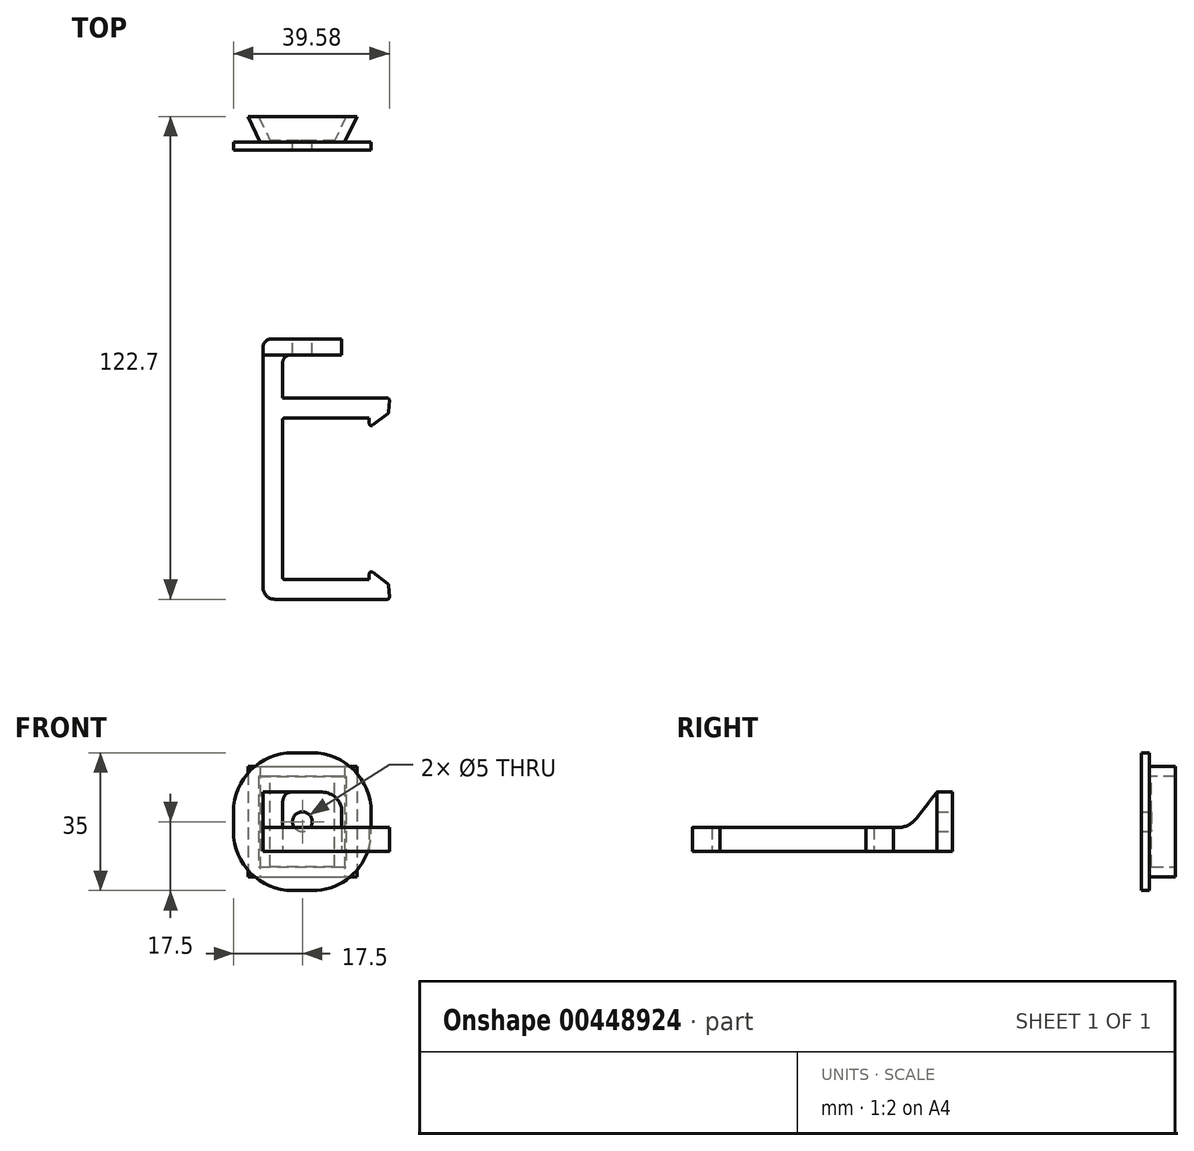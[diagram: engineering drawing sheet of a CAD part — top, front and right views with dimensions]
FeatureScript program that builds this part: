
annotation { "Feature Type Name" : "Feature", "Feature Type Description" : "" }
export const myFeature = defineFeature(function(context is Context, id is Id, definition is map)
    precondition{}
    {
        {
            var Q0;
            Q0=qCreatedBy(makeId("Top.planeOp"),FACE);
            var sketch = newSketch(context, id + "F0", { "sketchPlane" : qUnion([Q0])});
            skLineSegment(sketch, "E0.bottom", {"start": v(11, -20.55) * mm, "end": v(-11, -20.55) * mm});
            skLineSegment(sketch, "E0.top", {"start": v(11, 20.55) * mm, "end": v(-11, 20.55) * mm});
            skLineSegment(sketch, "E0.right", {"start": v(-11, -20.55) * mm, "end": v(-11, 20.55) * mm});
            skPoint(sketch, "E0.middle", {"position": v(0, 0) * mm});
            skLineSegment(sketch, "E1.0", {"start": v(11.44, -25.55) * mm, "end": v(-16, -25.55) * mm});
            skLineSegment(sketch, "E1.1", {"start": v(-16, -25.55) * mm, "end": v(-16, 25.55) * mm});
            skLineSegment(sketch, "E1.2", {"start": v(11.44, 25.55) * mm, "end": v(-16, 25.55) * mm});
            skLineSegment(sketch, "E2", {"start": v(11, 20.55) * mm, "end": v(11, 18.05) * mm});
            skLineSegment(sketch, "E3", {"start": v(11, 18.05) * mm, "end": v(20.79, 25.55) * mm});
            skLineSegment(sketch, "E4", {"start": v(20.79, 25.55) * mm, "end": v(11.44, 25.55) * mm});
            skLineSegment(sketch, "E5", {"start": v(-46.78, 0) * mm, "end": v(45.2, 0) * mm, "construction": true});
            skLineSegment(sketch, "E6.MirrorCS", {"start": v(11, -18.05) * mm, "end": v(20.79, -25.55) * mm});
            skLineSegment(sketch, "E7.MirrorCS", {"start": v(20.79, -25.55) * mm, "end": v(11.44, -25.55) * mm});
            skLineSegment(sketch, "E8.MirrorCS", {"start": v(11, -20.55) * mm, "end": v(11, -18.05) * mm});
            skLineSegment(sketch, "E9", {"start": v(16.11, 25.55) * mm, "end": v(15.9, 21.8) * mm});
            skLineSegment(sketch, "E10.MirrorCS", {"start": v(16.11, -25.55) * mm, "end": v(15.9, -21.8) * mm});
            skSolve(sketch);
        }
        {
            var Q0;
            Q0=makeQuery(id+"F0.imprint","IMPRINT",FACE,{"disambiguationData":[TD([[makeQuery(id+"F0.imprint","IMPRINT",EDGE,{"derivedFrom":sQuery(id+"F0.wireOp",EDGE,"E0.bottom")}),1.0]])]});
            extrude(context, id + "F1", {"entities" : qUnion([Q0]), "depth" : 6 * mm});
        }
        {
            var Q0;
            Q0=makeQuery(id+"F1.opExtrude","CAP_FACE",FACE,{"disambiguationData":[OSD([sQuery(id+"F0.wireOp",EDGE,"E0.bottom"),sQuery(id+"F0.wireOp",EDGE,"E0.top"),sQuery(id+"F0.wireOp",EDGE,"E0.right"),sQuery(id+"F0.wireOp",EDGE,"E1.0"),sQuery(id+"F0.wireOp",EDGE,"E1.1"),sQuery(id+"F0.wireOp",EDGE,"E1.2"),sQuery(id+"F0.wireOp",EDGE,"E2"),sQuery(id+"F0.wireOp",EDGE,"E3"),sQuery(id+"F0.wireOp",EDGE,"E4"),sQuery(id+"F0.wireOp",EDGE,"E6.MirrorCS"),sQuery(id+"F0.wireOp",EDGE,"E7.MirrorCS"),sQuery(id+"F0.wireOp",EDGE,"E8.MirrorCS")])],"isStart":true});
            var sketch = newSketch(context, id + "F2", { "sketchPlane" : qUnion([Q0])});
            skLineSegment(sketch, "E11.bottom", {"start": v(-16, -25.55) * mm, "end": v(-11, -25.55) * mm});
            skLineSegment(sketch, "E11.top", {"start": v(-16, -40.55) * mm, "end": v(-11, -40.55) * mm});
            skLineSegment(sketch, "E11.left", {"start": v(-16, -25.55) * mm, "end": v(-16, -40.55) * mm});
            skLineSegment(sketch, "E11.right", {"start": v(-11, -25.55) * mm, "end": v(-11, -36.55) * mm});
            skLineSegment(sketch, "E12.bottom", {"start": v(-11, -40.55) * mm, "end": v(4, -40.55) * mm});
            skLineSegment(sketch, "E12.top", {"start": v(-11, -36.55) * mm, "end": v(4, -36.55) * mm});
            skLineSegment(sketch, "E12.right", {"start": v(4, -40.55) * mm, "end": v(4, -36.55) * mm});
            skSolve(sketch);
        }
        {
            var Q0;
            Q0 = qSketchRegion(id + "F2", true);
            extrude(context, id + "F3", {"entities" : qUnion([Q0]), "operationType" : NewBodyOperationType.ADD, "oppositeDirection" : true, "depth" : 15 * mm});
        }
        {
            var Q0;
            Q0=makeQuery(id+"F3.opExtrude","SWEPT_FACE",FACE,{"disambiguationData":[OSD([sQuery(id+"F2.wireOp",EDGE,"E11.right")])]});
            var sketch = newSketch(context, id + "F4", { "sketchPlane" : qUnion([Q0])});
            skLineSegment(sketch, "E13", {"start": v(25.55, 6) * mm, "end": v(25.55, 15) * mm});
            skLineSegment(sketch, "E14", {"start": v(25.55, 15) * mm, "end": v(36.55, 15) * mm});
            skLineSegment(sketch, "E15", {"start": v(25.55, 6) * mm, "end": v(29.55, 6) * mm});
            skLineSegment(sketch, "E16", {"start": v(29.55, 6) * mm, "end": v(36.55, 15) * mm});
            skSolve(sketch);
        }
        {
            var Q0;
            Q0 = qSketchRegion(id + "F4", true);
            var Q1;
            Q1=makeQuery(id+"F3.boolean.opBoolean","MERGE",FACE,{"derivedFrom":[makeQuery(id+"F1.opExtrude","SWEPT_FACE",FACE,{"disambiguationData":[OSD([sQuery(id+"F0.wireOp",EDGE,"E1.1")])]}),makeQuery(id+"F3.opExtrude","SWEPT_FACE",FACE,{"disambiguationData":[OSD([sQuery(id+"F2.wireOp",EDGE,"E11.left")])]})]});
            extrude(context, id + "F5", {"entities" : qUnion([Q0]), "operationType" : NewBodyOperationType.REMOVE, "endBound" : BoundingType.UP_TO_SURFACE, "oppositeDirection" : true, "endBoundEntityFace" : qUnion([Q1]), "depth" : 25 * mm});
        }
        {
            var Q0;
            Q0=makeQuery(id+"F3.opExtrude","CAP_EDGE",EDGE,{"disambiguationData":[OSD([sQuery(id+"F2.wireOp",EDGE,"E12.right")])],"isStart":false});
            fillet(context, id + "F6", {"entities" : qUnion([Q0]), "radius" : 5 * mm, "tangentPropagation" : true, "allowEdgeOverflow" : false});
        }
        {
            var Q0;
            Q0=makeQuery(id+"F3.opExtrude","SWEPT_FACE",FACE,{"disambiguationData":[OSD([sQuery(id+"F2.wireOp",EDGE,"E11.top"),sQuery(id+"F2.wireOp",EDGE,"E12.bottom")])]});
            cPlane(context, id + "F7", {"entities" : qUnion([Q0]), "cplaneType" : CPlaneType.OFFSET, "offset" : 25 * mm, "width" : 150 * mm, "height" : 150 * mm});
        }
        {
            var Q0;
            Q0=makeQuery(id+"F3.opExtrude","SWEPT_FACE",FACE,{"disambiguationData":[OSD([sQuery(id+"F2.wireOp",EDGE,"E11.top"),sQuery(id+"F2.wireOp",EDGE,"E12.bottom")])]});
            cPlane(context, id + "F8", {"entities" : qUnion([Q0]), "cplaneType" : CPlaneType.OFFSET, "offset" : 48 * mm, "width" : 150 * mm, "height" : 150 * mm});
        }
        {
            var Q0;
            Q0=qCreatedBy(id+"F7.planeOp",FACE);
            var sketch = newSketch(context, id + "F9", { "sketchPlane" : qUnion([Q0])});
            skLineSegment(sketch, "E17.0.0", {"start": v(16, 15) * mm, "end": v(1, 15) * mm});
            skArc(sketch, "E17.0.1", {"start": v(1, 15) * mm, "mid": v(-2.54, 13.54) * mm, "end": v(-4, 10) * mm});
            skLineSegment(sketch, "E17.0.2", {"start": v(-4, 10) * mm, "end": v(-4, 0) * mm});
            skLineSegment(sketch, "E17.0.3", {"start": v(-4, 0) * mm, "end": v(16, 0) * mm});
            skLineSegment(sketch, "E17.0.4", {"start": v(16, 0) * mm, "end": v(16, 15) * mm});
            skSolve(sketch);
        }
        {
            var Q0;
            Q0=makeQuery(id+"F9.imprint","IMPRINT",FACE,{"disambiguationData":[TD([[makeQuery(id+"F9.imprint","IMPRINT",EDGE,{"derivedFrom":sQuery(id+"F9.wireOp",EDGE,"E17.0.0")}),1.0]])]});
            extrude(context, id + "F10", {"entities" : qUnion([Q0]), "depth" : 5 * mm});
        }
        {
            var Q0;
            Q0=qCreatedBy(id+"F8.planeOp",FACE);
            var sketch = newSketch(context, id + "F11", { "sketchPlane" : qUnion([Q0])});
            skLineSegment(sketch, "E18.bottom", {"start": v(23.5, -10) * mm, "end": v(-11.5, -10) * mm});
            skLineSegment(sketch, "E18.top", {"start": v(23.5, 25) * mm, "end": v(-11.5, 25) * mm});
            skLineSegment(sketch, "E18.left", {"start": v(23.5, -10) * mm, "end": v(23.5, 25) * mm});
            skLineSegment(sketch, "E18.right", {"start": v(-11.5, -10) * mm, "end": v(-11.5, 25) * mm});
            skPoint(sketch, "E18.middle", {"position": v(6, 7.5) * mm});
            skPoint(sketch, "E18.middle.positionSnap0", {"position": v(16, 7.5) * mm});
            skPoint(sketch, "E18.middle.positionSnap1", {"position": v(6, 0) * mm});
            skPoint(sketch, "E18.centerSnap0", {"position": v(16, 7.5) * mm});
            skPoint(sketch, "E18.centerSnap1", {"position": v(6, 0) * mm});
            skSolve(sketch);
        }
        {
            var Q0;
            Q0 = qSketchRegion(id + "F11", true);
            extrude(context, id + "F12", {"entities" : qUnion([Q0]), "operationType" : NewBodyOperationType.ADD, "depth" : 2 * mm});
        }
        {
            var Q0;
            Q0=makeQuery(id+"F12.opExtrude","CAP_FACE",FACE,{"disambiguationData":[OSD([sQuery(id+"F11.wireOp",EDGE,"E18.bottom"),sQuery(id+"F11.wireOp",EDGE,"E18.top"),sQuery(id+"F11.wireOp",EDGE,"E18.left"),sQuery(id+"F11.wireOp",EDGE,"E18.right")])],"isStart":false});
            var sketch = newSketch(context, id + "F13", { "sketchPlane" : qUnion([Q0])});
            skLineSegment(sketch, "E19.bottom", {"start": v(16.75, 21.5) * mm, "end": v(-4.75, 21.5) * mm});
            skLineSegment(sketch, "E19.top", {"start": v(16.75, -6.5) * mm, "end": v(-4.75, -6.5) * mm});
            skLineSegment(sketch, "E19.left", {"start": v(16.75, 21.5) * mm, "end": v(16.75, -6.5) * mm});
            skLineSegment(sketch, "E19.right", {"start": v(-4.75, 21.5) * mm, "end": v(-4.75, -6.5) * mm});
            skPoint(sketch, "E19.middle", {"position": v(6, 7.5) * mm});
            skPoint(sketch, "E19.middle.positionSnap0", {"position": v(-11.5, 7.5) * mm});
            skPoint(sketch, "E19.middle.positionSnap1", {"position": v(6, 25) * mm});
            skPoint(sketch, "E19.centerSnap0", {"position": v(-11.5, 7.5) * mm});
            skPoint(sketch, "E19.centerSnap1", {"position": v(6, 25) * mm});
            skSolve(sketch);
        }
        {
            var Q0;
            Q0=makeQuery(id+"F13.imprint","IMPRINT",FACE,{"disambiguationData":[TD([[makeQuery(id+"F13.imprint","IMPRINT",EDGE,{"derivedFrom":sQuery(id+"F13.wireOp",EDGE,"E19.bottom")}),1.0]])]});
            cPlane(context, id + "F14", {"entities" : qUnion([Q0]), "cplaneType" : CPlaneType.OFFSET, "offset" : 6.6 * mm, "width" : 150 * mm, "height" : 150 * mm});
        }
        {
            var Q0;
            Q0=qCreatedBy(id+"F14.planeOp",FACE);
            var sketch = newSketch(context, id + "F15", { "sketchPlane" : qUnion([Q0])});
            skLineSegment(sketch, "E20.0.0", {"start": v(-4.75, -6.5) * mm, "end": v(16.75, -6.5) * mm, "construction": true});
            skLineSegment(sketch, "E20.0.1", {"start": v(16.75, -6.5) * mm, "end": v(16.75, 21.5) * mm, "construction": true});
            skLineSegment(sketch, "E20.0.2", {"start": v(16.75, 21.5) * mm, "end": v(-4.75, 21.5) * mm, "construction": true});
            skLineSegment(sketch, "E20.0.3", {"start": v(-4.75, 21.5) * mm, "end": v(-4.75, -6.5) * mm, "construction": true});
            skLineSegment(sketch, "E21.bottom", {"start": v(19.85, 21.5) * mm, "end": v(-7.85, 21.5) * mm});
            skLineSegment(sketch, "E21.top", {"start": v(19.85, -6.5) * mm, "end": v(-7.85, -6.5) * mm});
            skLineSegment(sketch, "E21.left", {"start": v(19.85, 21.5) * mm, "end": v(19.85, -6.5) * mm});
            skLineSegment(sketch, "E21.right", {"start": v(-7.85, 21.5) * mm, "end": v(-7.85, -6.5) * mm});
            skPoint(sketch, "E21.middle", {"position": v(6, 7.5) * mm});
            skPoint(sketch, "E21.middle.positionSnap0", {"position": v(6, 21.5) * mm});
            skPoint(sketch, "E21.middle.positionSnap1", {"position": v(-4.75, 7.5) * mm});
            skPoint(sketch, "E21.centerSnap0", {"position": v(6, 21.5) * mm});
            skPoint(sketch, "E21.centerSnap1", {"position": v(-4.75, 7.5) * mm});
            skSolve(sketch);
        }
        {
            var Q2;
            Q2=makeQuery(id+"F15.imprint","IMPRINT",FACE,{"disambiguationData":[TD([[makeQuery(id+"F15.imprint","IMPRINT",EDGE,{"derivedFrom":sQuery(id+"F15.wireOp",EDGE,"E21.bottom")}),1.0]])]});
            var Q3;
            Q3=makeQuery(id+"F13.imprint","IMPRINT",FACE,{"disambiguationData":[TD([[makeQuery(id+"F13.imprint","IMPRINT",EDGE,{"derivedFrom":sQuery(id+"F13.wireOp",EDGE,"E19.bottom")}),1.0]])]});
            loft(context, id + "F16", {"operationType" : NewBodyOperationType.ADD, "sheetProfilesArray" : [{ "sheetProfileEntities" : qUnion([Q2]) }, { "sheetProfileEntities" : qUnion([Q3]) }]});
        }
        {
            var Q0;
            Q0=makeQuery(id+"F16.opLoft","CAP_FACE",FACE,{"disambiguationData":[OSD([makeQuery(id+"F15.imprint","IMPRINT",FACE,{"disambiguationData":[TD([[makeQuery(id+"F15.imprint","IMPRINT",EDGE,{"derivedFrom":sQuery(id+"F15.wireOp",EDGE,"E21.bottom")}),1.0]])]})])],"isStart":true});
            shell(context, id + "F17", {"entities" : qUnion([Q0]), "thickness" : 2.5 * mm});
        }
        {
            var Q0;
            Q0=makeQuery(id+"F10.opExtrude","SWEPT_BODY",BODY,{"disambiguationData":[OSD([sQuery(id+"F9.wireOp",EDGE,"E17.0.0"),sQuery(id+"F9.wireOp",EDGE,"E17.0.1"),sQuery(id+"F9.wireOp",EDGE,"E17.0.2"),sQuery(id+"F9.wireOp",EDGE,"E17.0.3"),sQuery(id+"F9.wireOp",EDGE,"E17.0.4")])]});
            deleteBodies(context, id + "F18", {"entities" : qUnion([Q0])});
        }
        {
            var Q0;
            Q0=makeQuery(id+"F17.opShell","OFFSET_FACE",FACE,{"disambiguationData":[OSD([sQuery(id+"F11.wireOp",EDGE,"E18.bottom"),sQuery(id+"F11.wireOp",EDGE,"E18.top"),sQuery(id+"F11.wireOp",EDGE,"E18.left"),sQuery(id+"F11.wireOp",EDGE,"E18.right")])]});
            var sketch = newSketch(context, id + "F19", { "sketchPlane" : qUnion([Q0])});
            skLineSegment(sketch, "E22.0.0", {"start": v(14.22, 19) * mm, "end": v(-2.22, 19) * mm, "construction": true});
            skLineSegment(sketch, "E22.0.1", {"start": v(-2.22, 19) * mm, "end": v(-2.22, -4) * mm, "construction": true});
            skLineSegment(sketch, "E22.0.2", {"start": v(-2.22, -4) * mm, "end": v(14.22, -4) * mm, "construction": true});
            skLineSegment(sketch, "E22.0.3", {"start": v(14.22, -4) * mm, "end": v(14.22, 19) * mm, "construction": true});
            skCircle(sketch, "E23", {"center": v(6, 7.5) * mm, "radius": 2.5 * mm});
            skPoint(sketch, "E23.centerSnap0", {"position": v(14.22, 7.5) * mm});
            skPoint(sketch, "E23.centerSnap1", {"position": v(6, 19) * mm});
            skSolve(sketch);
        }
        {
            var Q0;
            Q0 = qSketchRegion(id + "F19", true);
            var Q1;
            Q1=makeQuery(id+"F3.opExtrude","SWEPT_FACE",FACE,{"disambiguationData":[OSD([sQuery(id+"F2.wireOp",EDGE,"E12.top")])]});
            extrude(context, id + "F20", {"entities" : qUnion([Q0]), "operationType" : NewBodyOperationType.REMOVE, "endBound" : BoundingType.UP_TO_SURFACE, "oppositeDirection" : true, "endBoundEntityFace" : qUnion([Q1]), "depth" : 100 * mm});
        }
        {
            var Q0;
            Q0=makeQuery(id+"F12.opExtrude","SWEPT_EDGE",EDGE,{"disambiguationData":[OSD([sQuery(id+"F11.wireOp",EDGE,"E18.top"),sQuery(id+"F11.wireOp",EDGE,"E18.right")])]});
            var Q1;
            Q1=makeQuery(id+"F12.opExtrude","SWEPT_EDGE",EDGE,{"disambiguationData":[OSD([sQuery(id+"F11.wireOp",EDGE,"E18.top"),sQuery(id+"F11.wireOp",EDGE,"E18.left")])]});
            var Q2;
            Q2=makeQuery(id+"F12.opExtrude","SWEPT_EDGE",EDGE,{"disambiguationData":[OSD([sQuery(id+"F11.wireOp",EDGE,"E18.bottom"),sQuery(id+"F11.wireOp",EDGE,"E18.left")])]});
            var Q3;
            Q3=makeQuery(id+"F12.opExtrude","SWEPT_EDGE",EDGE,{"disambiguationData":[OSD([sQuery(id+"F11.wireOp",EDGE,"E18.bottom"),sQuery(id+"F11.wireOp",EDGE,"E18.right")])]});
            fillet(context, id + "F21", {"entities" : qUnion([Q0, Q1, Q2, Q3]), "radius" : 15 * mm, "tangentPropagation" : true, "allowEdgeOverflow" : false});
        }
        {
            var Q0;
            Q0=makeQuery(id+"F1.opExtrude","SWEPT_EDGE",EDGE,{"disambiguationData":[OSD([sQuery(id+"F0.wireOp",EDGE,"E1.0"),sQuery(id+"F0.wireOp",EDGE,"E1.1")])]});
            var Q1;
            {var subQ0=sQuery(id+"F0.wireOp",EDGE,"E4");var subQ1=sQuery(id+"F0.wireOp",EDGE,"E1.2");var subQ2=sQuery(id+"F2.wireOp",EDGE,"E11.right");Q1=makeQuery(id+"F3.boolean.opBoolean","SPLIT",EDGE,{"disambiguationData":[topologyDisambiguationEdgeConnected([makeQuery(id+"F1.opExtrude","SWEPT_FACE",FACE,{"disambiguationData":[OSD([subQ1,subQ0])]})])],"derivedFrom":makeQuery(id+"F3.opExtrude","SWEPT_EDGE",EDGE,{"disambiguationData":[OSD([subQ1,subQ0,sQuery(id+"F2.wireOp",EDGE,"E11.bottom"),subQ2])]})});}
            fillet(context, id + "F22", {"entities" : qUnion([Q0, Q1]), "radius" : 3 * mm, "tangentPropagation" : true, "allowEdgeOverflow" : false});
        }
        {
            var Q0;
            Q0=makeQuery(id+"F1.opExtrude","SWEPT_EDGE",EDGE,{"disambiguationData":[OSD([sQuery(id+"F0.wireOp",EDGE,"E3"),sQuery(id+"F0.wireOp",EDGE,"E4")])]});
            var Q1;
            Q1=makeQuery(id+"F1.opExtrude","SWEPT_EDGE",EDGE,{"disambiguationData":[OSD([sQuery(id+"F0.wireOp",EDGE,"E6.MirrorCS"),sQuery(id+"F0.wireOp",EDGE,"E7.MirrorCS")])]});
            var Q2;
            Q2=makeQuery(id+"F1.opExtrude","SWEPT_EDGE",EDGE,{"disambiguationData":[OSD([sQuery(id+"F0.wireOp",EDGE,"E6.MirrorCS"),sQuery(id+"F0.wireOp",EDGE,"E8.MirrorCS")])]});
            var Q3;
            Q3=makeQuery(id+"F1.opExtrude","SWEPT_EDGE",EDGE,{"disambiguationData":[OSD([sQuery(id+"F0.wireOp",EDGE,"E2"),sQuery(id+"F0.wireOp",EDGE,"E3")])]});
            var Q4;
            Q4=makeQuery(id+"F1.opExtrude","SWEPT_EDGE",EDGE,{"disambiguationData":[OSD([sQuery(id+"F0.wireOp",EDGE,"E0.top"),sQuery(id+"F0.wireOp",EDGE,"E0.right")])]});
            var Q5;
            Q5=makeQuery(id+"F1.opExtrude","SWEPT_EDGE",EDGE,{"disambiguationData":[OSD([sQuery(id+"F0.wireOp",EDGE,"E0.bottom"),sQuery(id+"F0.wireOp",EDGE,"E0.right")])]});
            fillet(context, id + "F23", {"entities" : qUnion([Q0, Q1, Q2, Q3, Q4, Q5]), "radius" : .5 * mm, "tangentPropagation" : true, "allowEdgeOverflow" : false});
        }
        {
            var Q0;
            Q0=makeQuery(id+"F3.opExtrude","SWEPT_EDGE",EDGE,{"disambiguationData":[OSD([sQuery(id+"F2.wireOp",EDGE,"E11.top"),sQuery(id+"F2.wireOp",EDGE,"E11.left")])]});
            var Q1;
            Q1=makeQuery(id+"F3.opExtrude","SWEPT_EDGE",EDGE,{"disambiguationData":[OSD([sQuery(id+"F2.wireOp",EDGE,"E11.right"),sQuery(id+"F2.wireOp",EDGE,"E12.top")])]});
            fillet(context, id + "F24", {"entities" : qUnion([Q0, Q1]), "radius" : 2 * mm, "tangentPropagation" : true, "allowEdgeOverflow" : false});
        }
        {
            var Q0;
            Q0=makeQuery(id+"F5.boolean.opBoolean","COPY",EDGE,{"derivedFrom":makeQuery(id+"F5.opExtrude","SWEPT_EDGE",EDGE,{"disambiguationData":[OSD([sQuery(id+"F4.wireOp",EDGE,"E15"),sQuery(id+"F4.wireOp",EDGE,"E16")])]})});
            fillet(context, id + "F25", {"entities" : qUnion([Q0]), "radius" : 6 * mm, "tangentPropagation" : true, "allowEdgeOverflow" : false});
        }
    });
